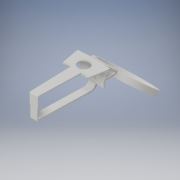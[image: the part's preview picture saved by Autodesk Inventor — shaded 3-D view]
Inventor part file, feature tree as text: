
AUTODESK INVENTOR PART (.ipt)
format: ipt  version: 2017 (Build 210142000, 142)  size: 1,414,144 bytes
history: native  units: mm
features: extrude x10, sketch x10, fillet x7, other x2, plane x1
ambient origin geometry x8: Origin, YZ Plane, XZ Plane, XY Plane, X Axis, Y Axis, Z Axis, Center Point
bodies: Body1 (feature_tree)
feature tree (30):
  extrude  "Extrusion2"  Depth=2.5mm TaperAngle=0.0deg
  extrude  "Extrusion3"  Depth=12.391838mm
  extrude  "Extrusion5"  Depth=28.099801mm
  plane  "Work Plane1"
  extrude  "Extrusion6"  Depth=6.5mm
  extrude  "Extrusion7"  Depth=3.5mm TaperAngle=0.0deg
  extrude  "Extrusion8"  Depth=2.5mm TaperAngle=0.0deg
  extrude  "Extrusion9"  Depth=2.5mm
  extrude  "Extrusion10"  Depth=2.5mm
  extrude  "Extrusion11"  Depth=22.863813mm
  fillet  "Fillet1"  Radius=4.0mm
  fillet  "Fillet3"  Radius=38.0mm
  fillet  "Fillet4"  Radius=10.0mm
  fillet  "Fillet5"  Radius=10.0mm
  fillet  "Fillet6"  Radius=1.4mm
  extrude  "Extrusion13"  Depth=0.45mm
  fillet  "Fillet8"  [1 undecoded]
  fillet  "Fillet9"  Radius=0.45mm
  sketch  "sketch1 - front_main"  dims[d66=26.0mm d67=12.391838mm]
  other  "Image1"
  sketch  "sketch2 - bottom_front_tab"  dims[d68=26.0mm d69=28.099801mm]
  sketch  "sketch3 - top_tab"  dims[d70=9.0mm d73=6.5mm]
  other  "Image2"
  sketch  "sketch5 - bottom_hinge"  dims[d74=6.5mm d76=3.5mm d77=0.0mm]
  sketch  "sketch6 - hinge_part"  dims[d82=17.0mm d88=2.5mm d89=0.0mm]
  sketch  "sketch7 - drink_arm"  dims[d90=12.789mm d91=0.0mm d92=2.5mm]
  sketch  "sketch8 - support_arm_arc_hole"  dims[d94=4.6mm d95=2.5mm]
  sketch  "sketch9 - cup_holder"  dims[d96=3.5mm d97=0.0mm d98=22.863813mm d99=4.0mm d100=38.0mm d101=0.0mm d106=10.0mm d107=0.0mm d109=10.0mm d110=0.0mm d111=1.4mm]
  sketch  "Sketch13"  dims[d12=2.5mm d13=0.0mm d18=2.5mm d19=0.0mm]
  sketch  "sketch4 - xbox_hole"  dims[d113=0.4mm d118=20.0mm d119=90.0deg d120=0.45mm d121=2.0mm d122=0.5mm d125=3.0mm d126=0.0mm d128=0.45mm d129=0.45mm]
note: 1 required parameter value undecoded (feature->parameter linkage not recoverable at this tier; creation-order binding heuristic only, values carry confidence <= 0.55)
